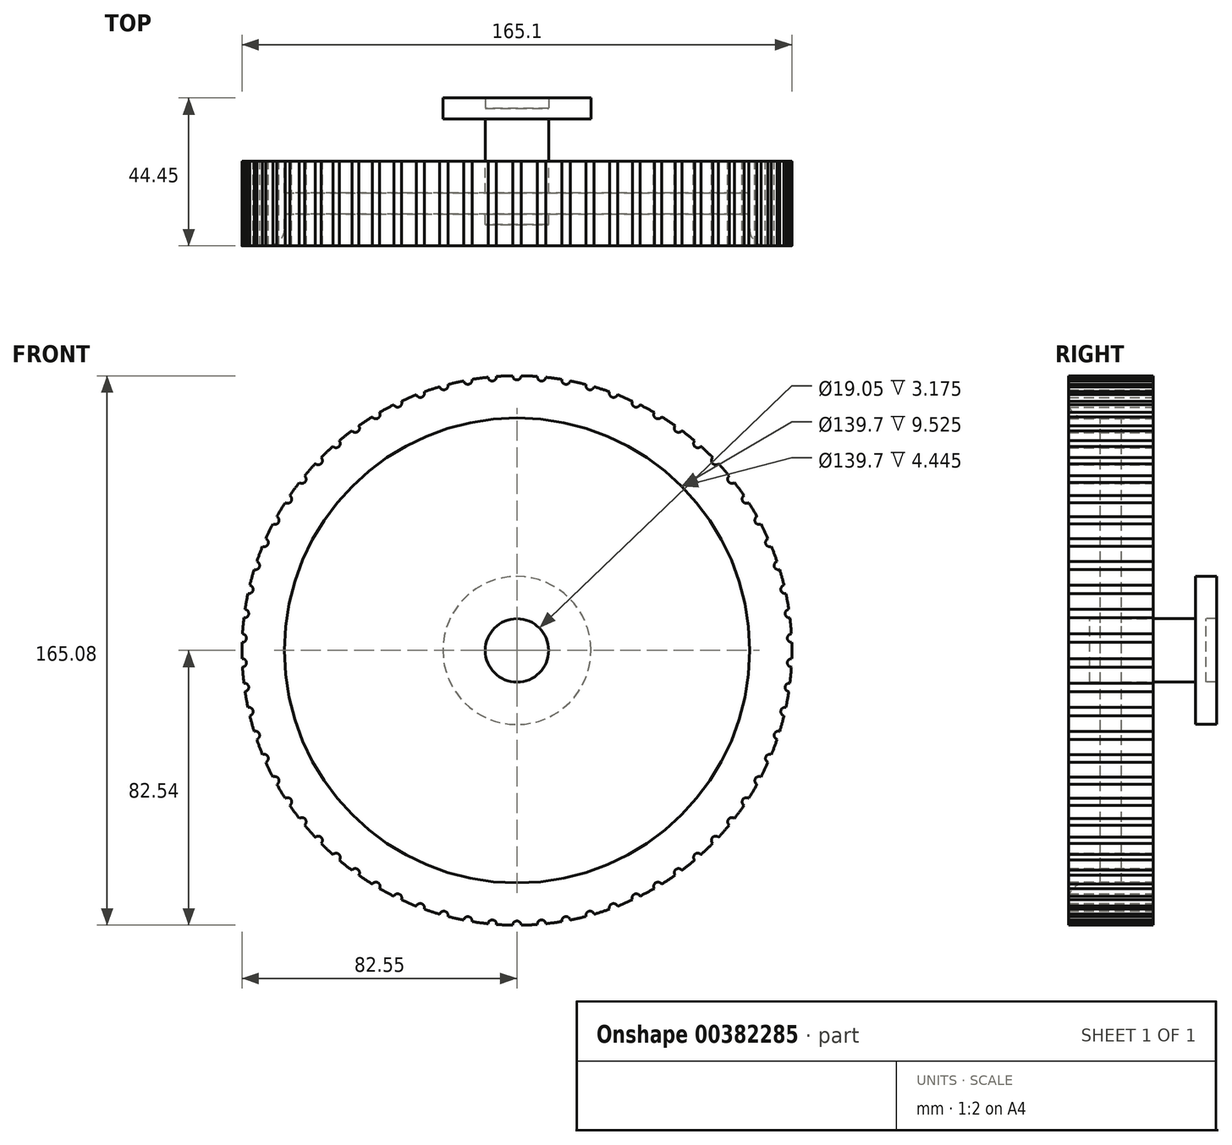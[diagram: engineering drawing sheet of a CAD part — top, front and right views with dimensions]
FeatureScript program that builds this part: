
annotation { "Feature Type Name" : "Feature", "Feature Type Description" : "" }
export const myFeature = defineFeature(function(context is Context, id is Id, definition is map)
    precondition{}
    {
        {
            var Q0;
            Q0=qCreatedBy(makeId("Front.planeOp"),FACE);
            var sketch = newSketch(context, id + "F0", { "sketchPlane" : qUnion([Q0])});
            skCircle(sketch, "E0", {"center": v(0, 0) * mm, "radius": 19.05 * mm});
            skCircle(sketch, "E1.0", {"center": v(0, 0) * mm, "radius": 22.23 * mm});
            skCircle(sketch, "E2", {"center": v(0, 0) * mm, "radius": 9.53 * mm});
            skSolve(sketch);
        }
        {
            var Q0;
            Q0=makeQuery(id+"F0.imprint","IMPRINT",FACE,{"disambiguationData":[TD([[makeQuery(id+"F0.imprint","IMPRINT",EDGE,{"derivedFrom":sQuery(id+"F0.wireOp",EDGE,"E0")}),-1.0]])]});
            extrude(context, id + "F1", {"entities" : qUnion([Q0]), "depth" : 6.35 * mm});
        }
        {
            var Q0;
            Q0=makeQuery(id+"F1.opExtrude","CAP_FACE",FACE,{"disambiguationData":[OSD([sQuery(id+"F0.wireOp",EDGE,"E0"),sQuery(id+"F0.wireOp",EDGE,"E1.0")])],"isStart":false});
            var sketch = newSketch(context, id + "F2", { "sketchPlane" : qUnion([Q0])});
            skCircle(sketch, "E3", {"center": v(0, 0) * mm, "radius": 22.23 * mm});
            skCircle(sketch, "E4", {"center": v(0, 0) * mm, "radius": 9.53 * mm});
            skSolve(sketch);
        }
        {
            var Q0;
            Q0=makeQuery(id+"F2.imprint","IMPRINT",FACE,{"disambiguationData":[TD([[makeQuery(id+"F2.imprint","IMPRINT",EDGE,{"derivedFrom":sQuery(id+"F2.wireOp",EDGE,"E4")}),1.0]])]});
            extrude(context, id + "F3", {"entities" : qUnion([Q0]), "depth" : 25.4 * mm});
        }
        {
            var Q0;
            Q0=makeQuery(id+"F2.imprint","IMPRINT",FACE,{"disambiguationData":[TD([[makeQuery(id+"F2.imprint","IMPRINT",EDGE,{"derivedFrom":sQuery(id+"F2.wireOp",EDGE,"E4")}),-1.0]])]});
            var Q1;
            Q1=makeQuery(id+"F2.imprint","IMPRINT",FACE,{"disambiguationData":[TD([[makeQuery(id+"F2.imprint","IMPRINT",EDGE,{"derivedFrom":sQuery(id+"F2.wireOp",EDGE,"E3")}),1.0]])]});
            extrude(context, id + "F4", {"entities" : qUnion([Q0, Q1]), "operationType" : NewBodyOperationType.ADD, "oppositeDirection" : true, "depth" : 6.35 * mm});
        }
        {
            var Q0;
            Q0=makeQuery(id+"F2.imprint","IMPRINT",FACE,{"disambiguationData":[TD([[makeQuery(id+"F2.imprint","IMPRINT",EDGE,{"derivedFrom":sQuery(id+"F2.wireOp",EDGE,"E4")}),1.0]])]});
            extrude(context, id + "F5", {"entities" : qUnion([Q0]), "operationType" : NewBodyOperationType.ADD, "oppositeDirection" : true, "depth" : 3.17 * mm});
        }
        {
            var Q0;
            Q0=makeQuery(id+"F3.opExtrude","CAP_FACE",FACE,{"disambiguationData":[OSD([sQuery(id+"F2.wireOp",EDGE,"E4")])],"isStart":false});
            var sketch = newSketch(context, id + "F6", { "sketchPlane" : qUnion([Q0])});
            skCircle(sketch, "E5", {"center": v(0, 0) * mm, "radius": 82.55 * mm});
            skCircle(sketch, "E6.0", {"center": v(0, 0) * mm, "radius": 69.85 * mm});
            skArc(sketch, "E7", {"start": v(1.27, 82.54) * mm, "mid": v(0, 81.28) * mm, "end": v(-1.27, 82.54) * mm});
            skArc(sketch, "E8", {"start": v(-1.27, 82.54) * mm, "mid": v(0.64, -82.55) * mm, "end": v(0, 82.55) * mm});
            skArc(sketch, "E9.1.0", {"start": v(-6.13, 82.32) * mm, "mid": v(-7.29, 80.95) * mm, "end": v(-8.66, 82.1) * mm});
            skArc(sketch, "E9.2.0", {"start": v(-13.49, 81.44) * mm, "mid": v(-14.51, 79.97) * mm, "end": v(-15.99, 80.99) * mm});
            skArc(sketch, "E10.3.3.0", {"start": v(-20.73, 79.9) * mm, "mid": v(-21.62, 78.35) * mm, "end": v(-23.18, 79.23) * mm});
            skArc(sketch, "E10.3.4.0", {"start": v(-27.81, 77.72) * mm, "mid": v(-28.56, 76.1) * mm, "end": v(-30.2, 76.83) * mm});
            skArc(sketch, "E11.3.5.0", {"start": v(-34.67, 74.92) * mm, "mid": v(-35.27, 73.23) * mm, "end": v(-36.96, 73.82) * mm});
            skArc(sketch, "E11.3.6.0", {"start": v(-41.24, 71.5) * mm, "mid": v(-41.69, 69.77) * mm, "end": v(-43.43, 70.2) * mm});
            skArc(sketch, "E11.3.7.0", {"start": v(-47.49, 67.52) * mm, "mid": v(-47.78, 65.76) * mm, "end": v(-49.54, 66.03) * mm});
            skArc(sketch, "E11.3.8.0", {"start": v(-53.35, 63) * mm, "mid": v(-53.48, 61.2) * mm, "end": v(-55.26, 61.32) * mm});
            skArc(sketch, "E11.3.9.0", {"start": v(-58.78, 57.96) * mm, "mid": v(-58.75, 56.17) * mm, "end": v(-60.54, 56.12) * mm});
            skArc(sketch, "E11.3.10.0", {"start": v(-63.74, 52.46) * mm, "mid": v(-63.55, 50.68) * mm, "end": v(-65.32, 50.47) * mm});
            skArc(sketch, "E11.3.11.0", {"start": v(-68.19, 46.53) * mm, "mid": v(-67.83, 44.78) * mm, "end": v(-69.59, 44.41) * mm});
            skArc(sketch, "E11.3.12.0", {"start": v(-72.08, 40.23) * mm, "mid": v(-71.57, 38.52) * mm, "end": v(-73.29, 38) * mm});
            skArc(sketch, "E11.3.13.0", {"start": v(-75.4, 33.6) * mm, "mid": v(-74.74, 31.95) * mm, "end": v(-76.4, 31.27) * mm});
            skArc(sketch, "E11.3.14.0", {"start": v(-78.1, 26.71) * mm, "mid": v(-77.3, 25.12) * mm, "end": v(-78.9, 24.3) * mm});
            skArc(sketch, "E11.3.15.0", {"start": v(-80.19, 19.6) * mm, "mid": v(-79.24, 18.09) * mm, "end": v(-80.75, 17.13) * mm});
            skArc(sketch, "E11.3.16.0", {"start": v(-81.62, 12.34) * mm, "mid": v(-80.54, 10.91) * mm, "end": v(-81.96, 9.82) * mm});
            skArc(sketch, "E11.3.17.0", {"start": v(-82.4, 4.97) * mm, "mid": v(-81.2, 3.65) * mm, "end": v(-82.51, 2.43) * mm});
            skArc(sketch, "E11.3.18.0", {"start": v(-82.51, -2.43) * mm, "mid": v(-81.2, -3.65) * mm, "end": v(-82.4, -4.97) * mm});
            skArc(sketch, "E11.3.19.0", {"start": v(-81.96, -9.82) * mm, "mid": v(-80.54, -10.91) * mm, "end": v(-81.62, -12.34) * mm});
            skArc(sketch, "E11.3.20.0", {"start": v(-80.75, -17.13) * mm, "mid": v(-79.24, -18.09) * mm, "end": v(-80.19, -19.6) * mm});
            skArc(sketch, "E11.3.21.0", {"start": v(-78.9, -24.3) * mm, "mid": v(-77.3, -25.12) * mm, "end": v(-78.1, -26.71) * mm});
            skArc(sketch, "E11.3.22.0", {"start": v(-76.4, -31.27) * mm, "mid": v(-74.74, -31.95) * mm, "end": v(-75.4, -33.6) * mm});
            skArc(sketch, "E11.3.23.0", {"start": v(-73.29, -38) * mm, "mid": v(-71.57, -38.52) * mm, "end": v(-72.08, -40.23) * mm});
            skArc(sketch, "E11.3.24.0", {"start": v(-69.59, -44.41) * mm, "mid": v(-67.83, -44.78) * mm, "end": v(-68.19, -46.53) * mm});
            skArc(sketch, "E11.3.25.0", {"start": v(-65.32, -50.47) * mm, "mid": v(-63.55, -50.68) * mm, "end": v(-63.74, -52.46) * mm});
            skArc(sketch, "E11.3.26.0", {"start": v(-60.54, -56.12) * mm, "mid": v(-58.75, -56.17) * mm, "end": v(-58.78, -57.96) * mm});
            skArc(sketch, "E11.3.27.0", {"start": v(-55.26, -61.32) * mm, "mid": v(-53.48, -61.2) * mm, "end": v(-53.35, -63) * mm});
            skArc(sketch, "E11.3.28.0", {"start": v(-49.54, -66.03) * mm, "mid": v(-47.78, -65.76) * mm, "end": v(-47.49, -67.52) * mm});
            skArc(sketch, "E11.3.29.0", {"start": v(-43.43, -70.2) * mm, "mid": v(-41.69, -69.77) * mm, "end": v(-41.24, -71.5) * mm});
            skArc(sketch, "E12.3.30.0", {"start": v(-36.96, -73.82) * mm, "mid": v(-35.27, -73.23) * mm, "end": v(-34.67, -74.92) * mm});
            skArc(sketch, "E12.3.31.0", {"start": v(-30.2, -76.83) * mm, "mid": v(-28.56, -76.1) * mm, "end": v(-27.81, -77.72) * mm});
            skArc(sketch, "E12.3.32.0", {"start": v(-23.18, -79.23) * mm, "mid": v(-21.62, -78.35) * mm, "end": v(-20.73, -79.9) * mm});
            skArc(sketch, "E12.3.33.0", {"start": v(-15.99, -80.99) * mm, "mid": v(-14.51, -79.97) * mm, "end": v(-13.49, -81.44) * mm});
            skArc(sketch, "E12.3.34.0", {"start": v(-8.66, -82.1) * mm, "mid": v(-7.29, -80.95) * mm, "end": v(-6.13, -82.32) * mm});
            skArc(sketch, "E12.3.35.0", {"start": v(-1.27, -82.54) * mm, "mid": v(0, -81.28) * mm, "end": v(1.27, -82.54) * mm});
            skArc(sketch, "E12.3.36.0", {"start": v(6.13, -82.32) * mm, "mid": v(7.29, -80.95) * mm, "end": v(8.66, -82.1) * mm});
            skArc(sketch, "E12.3.37.0", {"start": v(13.49, -81.44) * mm, "mid": v(14.51, -79.97) * mm, "end": v(15.99, -80.99) * mm});
            skArc(sketch, "E12.3.38.0", {"start": v(20.73, -79.9) * mm, "mid": v(21.62, -78.35) * mm, "end": v(23.18, -79.23) * mm});
            skArc(sketch, "E12.3.39.0", {"start": v(27.81, -77.72) * mm, "mid": v(28.56, -76.1) * mm, "end": v(30.2, -76.83) * mm});
            skArc(sketch, "E12.3.40.0", {"start": v(34.67, -74.92) * mm, "mid": v(35.27, -73.23) * mm, "end": v(36.96, -73.82) * mm});
            skArc(sketch, "E12.3.41.0", {"start": v(41.24, -71.5) * mm, "mid": v(41.69, -69.77) * mm, "end": v(43.43, -70.2) * mm});
            skArc(sketch, "E12.3.42.0", {"start": v(47.49, -67.52) * mm, "mid": v(47.78, -65.76) * mm, "end": v(49.54, -66.03) * mm});
            skArc(sketch, "E12.3.43.0", {"start": v(53.35, -63) * mm, "mid": v(53.48, -61.2) * mm, "end": v(55.26, -61.32) * mm});
            skArc(sketch, "E12.3.44.0", {"start": v(58.78, -57.96) * mm, "mid": v(58.75, -56.17) * mm, "end": v(60.54, -56.12) * mm});
            skArc(sketch, "E13.3.45.0", {"start": v(63.74, -52.46) * mm, "mid": v(63.55, -50.68) * mm, "end": v(65.32, -50.47) * mm});
            skArc(sketch, "E13.3.46.0", {"start": v(68.19, -46.53) * mm, "mid": v(67.83, -44.78) * mm, "end": v(69.59, -44.41) * mm});
            skArc(sketch, "E13.3.47.0", {"start": v(72.08, -40.23) * mm, "mid": v(71.57, -38.52) * mm, "end": v(73.29, -38) * mm});
            skArc(sketch, "E13.3.48.0", {"start": v(75.4, -33.6) * mm, "mid": v(74.74, -31.95) * mm, "end": v(76.4, -31.27) * mm});
            skArc(sketch, "E13.3.49.0", {"start": v(78.1, -26.71) * mm, "mid": v(77.3, -25.12) * mm, "end": v(78.9, -24.3) * mm});
            skArc(sketch, "E13.3.50.0", {"start": v(80.19, -19.6) * mm, "mid": v(79.24, -18.09) * mm, "end": v(80.75, -17.13) * mm});
            skArc(sketch, "E13.3.51.0", {"start": v(81.62, -12.34) * mm, "mid": v(80.54, -10.91) * mm, "end": v(81.96, -9.82) * mm});
            skArc(sketch, "E13.3.52.0", {"start": v(82.4, -4.97) * mm, "mid": v(81.2, -3.65) * mm, "end": v(82.51, -2.43) * mm});
            skArc(sketch, "E13.3.53.0", {"start": v(82.51, 2.43) * mm, "mid": v(81.2, 3.65) * mm, "end": v(82.4, 4.97) * mm});
            skArc(sketch, "E13.3.54.0", {"start": v(81.96, 9.82) * mm, "mid": v(80.54, 10.91) * mm, "end": v(81.62, 12.34) * mm});
            skArc(sketch, "E13.3.55.0", {"start": v(80.75, 17.13) * mm, "mid": v(79.24, 18.09) * mm, "end": v(80.19, 19.6) * mm});
            skArc(sketch, "E13.3.56.0", {"start": v(78.9, 24.3) * mm, "mid": v(77.3, 25.12) * mm, "end": v(78.1, 26.71) * mm});
            skArc(sketch, "E13.3.57.0", {"start": v(76.4, 31.27) * mm, "mid": v(74.74, 31.95) * mm, "end": v(75.4, 33.6) * mm});
            skArc(sketch, "E13.3.58.0", {"start": v(73.29, 38) * mm, "mid": v(71.57, 38.52) * mm, "end": v(72.08, 40.23) * mm});
            skArc(sketch, "E13.3.59.0", {"start": v(69.59, 44.41) * mm, "mid": v(67.83, 44.78) * mm, "end": v(68.19, 46.53) * mm});
            skArc(sketch, "E14.3.60.0", {"start": v(65.32, 50.47) * mm, "mid": v(63.55, 50.68) * mm, "end": v(63.74, 52.46) * mm});
            skArc(sketch, "E14.3.61.0", {"start": v(60.54, 56.12) * mm, "mid": v(58.75, 56.17) * mm, "end": v(58.78, 57.96) * mm});
            skArc(sketch, "E14.3.62.0", {"start": v(55.26, 61.32) * mm, "mid": v(53.48, 61.2) * mm, "end": v(53.35, 63) * mm});
            skArc(sketch, "E14.3.63.0", {"start": v(49.54, 66.03) * mm, "mid": v(47.78, 65.76) * mm, "end": v(47.49, 67.52) * mm});
            skArc(sketch, "E14.3.64.0", {"start": v(43.43, 70.2) * mm, "mid": v(41.69, 69.77) * mm, "end": v(41.24, 71.5) * mm});
            skArc(sketch, "E15.3.65.0", {"start": v(36.96, 73.82) * mm, "mid": v(35.27, 73.23) * mm, "end": v(34.67, 74.92) * mm});
            skArc(sketch, "E15.3.66.0", {"start": v(30.2, 76.83) * mm, "mid": v(28.56, 76.1) * mm, "end": v(27.81, 77.72) * mm});
            skArc(sketch, "E15.3.67.0", {"start": v(23.18, 79.23) * mm, "mid": v(21.62, 78.35) * mm, "end": v(20.73, 79.9) * mm});
            skArc(sketch, "E15.3.68.0", {"start": v(15.99, 80.99) * mm, "mid": v(14.51, 79.97) * mm, "end": v(13.49, 81.44) * mm});
            skArc(sketch, "E15.3.69.0", {"start": v(8.66, 82.1) * mm, "mid": v(7.29, 80.95) * mm, "end": v(6.13, 82.32) * mm});
            skSolve(sketch);
        }
        {
            var Q0;
            Q0=makeQuery(id+"F6.imprint","IMPRINT",FACE,{"disambiguationData":[TD([[makeQuery(id+"F6.imprint","IMPRINT",EDGE,{"derivedFrom":sQuery(id+"F6.wireOp",EDGE,"E6.0")}),-1.0]])]});
            extrude(context, id + "F7", {"entities" : qUnion([Q0]), "endBound" : BoundingType.SYMMETRIC, "depth" : 25.4 * mm});
        }
        {
            var Q0;
            Q0=makeQuery(id+"F6.imprint","IMPRINT",FACE,{"disambiguationData":[TD([[makeQuery(id+"F6.imprint","IMPRINT",EDGE,{"derivedFrom":sQuery(id+"F6.wireOp",EDGE,"E6.0")}),1.0]])]});
            extrude(context, id + "F8", {"entities" : qUnion([Q0]), "operationType" : NewBodyOperationType.ADD, "endBound" : BoundingType.SYMMETRIC, "depth" : 6.35 * mm});
        }
        {
            var Q0;
            Q0=makeQuery(id+"F6.imprint","IMPRINT",FACE,{"disambiguationData":[TD([[makeQuery(id+"F6.imprint","IMPRINT",EDGE,{"derivedFrom":makeQuery(id+"F3.opExtrude","CAP_EDGE",EDGE,{"disambiguationData":[OSD([sQuery(id+"F2.wireOp",EDGE,"E4")])],"isStart":false})}),1.0]])]});
            extrude(context, id + "F9", {"entities" : qUnion([Q0]), "operationType" : NewBodyOperationType.ADD, "depth" : 6.35 * mm});
        }
        {
            var Q0;
            Q0=makeQuery(id+"F7.opExtrude","CAP_EDGE",EDGE,{"disambiguationData":[OSD([sQuery(id+"F6.wireOp",EDGE,"E6.0")])],"isStart":false});
            fillet(context, id + "F10", {"entities" : qUnion([Q0]), "radius" : 5.08 * mm, "tangentPropagation" : true, "allowEdgeOverflow" : false});
        }
    });
